FCSTD DOCUMENT  (FreeCAD 2023.731R38791 (Git))
Label: UR5e_asm
License: All rights reserved
LicenseURL: http://en.wikipedia.org/wiki/All_rights_reserved
objects: App::Link×17, App::DocumentObjectGroup×3, PartDesign::CoordinateSystem×1, App::FeaturePython×1, App::Part×1, TechDraw::DrawSVGTemplate×1, TechDraw::DrawViewPart×1, TechDraw::DrawPage×1
note: 1 computed .brp shape members not serialized (recipe doc carries the construction recipe); baked Part::Feature solids carry a one-line shape summary decoded from their .brp
EXTERNAL_REF file=parts/Hub_Offset_asm.FCStd obj=Group_Shaft
EXTERNAL_REF file=Joint_mount.FCStd obj=Hub_Bore
EXTERNAL_REF file=parts/Hub_Offset_asm.FCStd obj=Assembly
EXTERNAL_REF file=parts/Hub_Offset_asm.FCStd obj=Group_Bore0
EXTERNAL_REF file=prefab/Interconnect_shaft.FCStd obj=Local_CS
EXTERNAL_REF file=prefab/Interconnect_shaft.FCStd obj=Icon_Shaft
EXTERNAL_REF file=parts/Hub_Offset_asm.FCStd obj=Group_Bore1
EXTERNAL_REF file=parts/Hub_Mount_asm.FCStd obj=Hub_Mount_Bore1
EXTERNAL_REF file=prefab/Interconnect_shaft.FCStd obj=Local_CS001
EXTERNAL_REF file=parts/Hub_Mount_asm.FCStd obj=Assembly
EXTERNAL_REF file=parts/Hub_Mount_asm.FCStd obj=Group_Base
EXTERNAL_REF file=Joint_mount.FCStd obj=Encoder_Base
EXTERNAL_REF file=Joint_mount.FCStd obj=Assembly
EXTERNAL_REF file=parts/Hub_Offset_Direct_asm.FCStd obj=DIrect_Mount
EXTERNAL_REF file=parts/Hub_Offset_Direct_asm.FCStd obj=Assembly
EXTERNAL_REF file=parts/Hub_Offset_Direct_asm.FCStd obj=DIrect_ASM_mount
EXTERNAL_REF file=Joint_mount.FCStd obj=LCS_Origin
EXTERNAL_REF file=parts/Hub_Mount_asm.FCStd obj=Hub_Mount_Bore0

FEATURE [App::DocumentObjectGroup] Parts
  ClaimAllChildren = true
  ExportMode = 1
  TreeRank = 0
  _GroupVersion = 1
FEATURE [PartDesign::CoordinateSystem] LCS_Origin
  AttacherType = Attacher::AttachEngine3D
  AttachmentSupport = -> [X_Axis]
  InvalidShape = false
  MapMode = 2
  Support = -> [X_Axis]
  TreeRank = 0
  ValidateShape = false
FEATURE [App::DocumentObjectGroup] Constraints
  ClaimAllChildren = true
  ExportMode = 1
  TreeRank = 0
  _GroupVersion = 1
FEATURE [App::FeaturePython] Variables  # WARN: FeaturePython — macro-defined, semantics opaque (R4)
  TreeRank = 0
  Type = App::PropertyContainer
FEATURE [App::DocumentObjectGroup] Configurations
  ClaimAllChildren = true
  ExportMode = 1
  TreeRank = 0
  _GroupVersion = 1
FEATURE [App::Link] Hub_offset_asm001  label="Hub_offset_asm"
  AttachedBy = #Group_Shaft
  AttachedTo = Joint_mount001#Hub_Bore
  AttachmentOffset = pos=(0,0,0) rot=(0,0,1;3.14159rad)
  AutoLinkLabel = true
  AutoPlacement = true
  LinkPlacement = pos=(-17,-235,-0.999989) rot=(0.57735,-0.57735,0.57735;4.18879rad)
  LinkedObject = -> <external parts/Hub_Offset_asm.FCStd>#Assembly
  Placement = pos=(-17,-235,-0.999989) rot=(0.57735,-0.57735,0.57735;4.18879rad)
  SolverId = Asm4EE
  SyncGroupVisibility = false
  TreeRank = 7
  _LinkVersion = 1
  expr: Placement = Joint_mount001.Placement * Joint_mount#Hub_Bore.Placement * AttachmentOffset * Hub_Offset_asm#Group_Shaft.Placement ^ (-1)
FEATURE [App::Link] Icon_Shaft002  label="Icon_Shaft002(Icon_Shaft)"
  AttachedBy = #Local_CS
  AttachedTo = Hub_offset_asm001#Group_Bore0
  AutoLinkLabel = true
  AutoPlacement = true
  LinkPlacement = pos=(-9.50001,-217,-18) rot=(1,0,0;1.5708rad)
  LinkedObject = -> <external prefab/Interconnect_shaft.FCStd>#Icon_Shaft
  Placement = pos=(-9.50001,-217,-18) rot=(1,0,0;1.5708rad)
  SolverId = Asm4EE
  SyncGroupVisibility = false
  TreeRank = 8
  _LinkVersion = 1
  expr: Placement = Hub_offset_asm001.Placement * Hub_Offset_asm#Group_Bore0.Placement * AttachmentOffset * Interconnect_shaft#Local_CS.Placement ^ (-1)
FEATURE [App::Link] Icon_Shaft002_Icon_Shaft_  label="Icon_Shaft002(Icon_Shaft)001"
  AttachedBy = #Local_CS
  AttachedTo = Hub_offset_asm001#Group_Bore1
  AutoLinkLabel = true
  AutoPlacement = true
  LinkPlacement = pos=(-9.49999,-217,16) rot=(1,0,0;1.5708rad)
  LinkedObject = -> <external prefab/Interconnect_shaft.FCStd>#Icon_Shaft
  Placement = pos=(-9.49999,-217,16) rot=(1,0,0;1.5708rad)
  SolverId = Asm4EE
  SyncGroupVisibility = false
  TreeRank = 9
  _LinkVersion = 1
  expr: Placement = Hub_offset_asm001.Placement * Hub_Offset_asm#Group_Bore1.Placement * AttachmentOffset * Interconnect_shaft#Local_CS.Placement ^ (-1)
FEATURE [App::Link] Hub_Mount_asm001  label="Hub_Mount_asm"
  AttachedBy = #Hub_Mount_Bore1
  AttachedTo = Icon_Shaft002_Icon_Shaft_#Local_CS001
  AttachmentOffset = pos=(0,0,0) rot=(0,0,1;1.5708rad)
  AutoLinkLabel = true
  AutoPlacement = true
  LinkPlacement = pos=(8.99999e-06,-371,14) rot=(0,-1,0;4.71239rad)
  LinkedObject = -> <external parts/Hub_Mount_asm.FCStd>#Assembly
  Placement = pos=(8.99999e-06,-371,14) rot=(0,-1,0;4.71239rad)
  SolverId = Asm4EE
  SyncGroupVisibility = false
  TreeRank = 10
  _LinkVersion = 1
  expr: Placement = Icon_Shaft002_Icon_Shaft_.Placement * Interconnect_shaft#Local_CS001.Placement * AttachmentOffset * Hub_Mount_asm#Hub_Mount_Bore1.Placement ^ (-1)
FEATURE [App::Link] Joint_mount003  label="Joint_mount003(Assembly)"
  AttachedBy = #Encoder_Base
  AttachedTo = Hub_Mount_asm001#Group_Base
  AttachmentOffset = pos=(0,0,0) rot=(0,0,1;4.71239rad)
  AutoLinkLabel = true
  AutoPlacement = true
  LinkPlacement = pos=(4,-388,0.499997) rot=(0.57735,0.57735,-0.57735;2.0944rad)
  LinkedObject = -> <external Joint_mount.FCStd>#Assembly
  Placement = pos=(4,-388,0.499997) rot=(0.57735,0.57735,-0.57735;2.0944rad)
  SolverId = Asm4EE
  SyncGroupVisibility = false
  TreeRank = 16
  _LinkVersion = 1
  expr: Placement = Hub_Mount_asm001.Placement * Hub_Mount_asm#Group_Base.Placement * AttachmentOffset * Joint_mount#Encoder_Base.Placement ^ (-1)
FEATURE [App::Link] Direct_asm  label="Direct_asm(Direct_asm)"
  AttachedBy = #DIrect_Mount
  AttachedTo = Joint_mount003#Hub_Bore
  AutoLinkLabel = true
  AutoPlacement = true
  LinkPlacement = pos=(-53,-388,20.5) rot=(-0.57735,-0.57735,0.57735;2.09439rad)
  LinkedObject = -> <external parts/Hub_Offset_Direct_asm.FCStd>#Assembly
  Placement = pos=(-53,-388,20.5) rot=(-0.57735,-0.57735,0.57735;2.09439rad)
  SolverId = Asm4EE
  SyncGroupVisibility = false
  TreeRank = 19
  _LinkVersion = 1
  expr: Placement = Joint_mount003.Placement * Joint_mount#Hub_Bore.Placement * AttachmentOffset * Hub_Offset_Direct_asm#DIrect_Mount.Placement ^ (-1)
FEATURE [App::Link] Joint_mount004  label="Joint_mount004(Assembly)"
  AttachedBy = #Encoder_Base
  AttachedTo = Direct_asm#DIrect_ASM_mount
  AutoLinkLabel = true
  AutoPlacement = true
  LinkPlacement = pos=(-78,-388.5,-3.49995) rot=(-0.57735,-0.57735,0.57735;2.09439rad)
  LinkedObject = -> <external Joint_mount.FCStd>#Assembly
  Placement = pos=(-78,-388.5,-3.49995) rot=(-0.57735,-0.57735,0.57735;2.09439rad)
  SolverId = Asm4EE
  SyncGroupVisibility = false
  TreeRank = 20
  _LinkVersion = 1
  expr: Placement = Direct_asm.Placement * Hub_Offset_Direct_asm#DIrect_ASM_mount.Placement * AttachmentOffset * Joint_mount#Encoder_Base.Placement ^ (-1)
FEATURE [App::Link] Direct_asm001  label="Direct_asm"
  AttachedBy = #DIrect_Mount
  AttachedTo = Joint_mount004#Hub_Bore
  AutoLinkLabel = true
  AutoPlacement = true
  LinkPlacement = pos=(-78,-408.5,53.5) rot=(-0.57735,-0.57735,0.57735;6.28318rad)
  LinkedObject = -> <external parts/Hub_Offset_Direct_asm.FCStd>#Assembly
  Placement = pos=(-78,-408.5,53.5) rot=(-0.57735,-0.57735,0.57735;6.28318rad)
  SolverId = Asm4EE
  SyncGroupVisibility = false
  TreeRank = 21
  _LinkVersion = 1
  expr: Placement = Joint_mount004.Placement * Joint_mount#Hub_Bore.Placement * AttachmentOffset * Hub_Offset_Direct_asm#DIrect_Mount.Placement ^ (-1)
FEATURE [App::Link] Joint_mount005  label="Joint_mount005(Assembly)"
  AttachedBy = #Encoder_Base
  AttachedTo = Direct_asm001#DIrect_ASM_mount
  AutoLinkLabel = true
  AutoPlacement = true
  LinkPlacement = pos=(-78.4999,-384.5,78.5001) rot=(-0.57735,-0.57735,0.57735;6.28318rad)
  LinkedObject = -> <external Joint_mount.FCStd>#Assembly
  Placement = pos=(-78.4999,-384.5,78.5001) rot=(-0.57735,-0.57735,0.57735;6.28318rad)
  SolverId = Asm4EE
  SyncGroupVisibility = false
  TreeRank = 22
  _LinkVersion = 1
  expr: Placement = Direct_asm001.Placement * Hub_Offset_Direct_asm#DIrect_ASM_mount.Placement * AttachmentOffset * Joint_mount#Encoder_Base.Placement ^ (-1)
FEATURE [App::Link] Joint_mount006  label="Joint_mount006(Assembly)"
  AttachedBy = #LCS_Origin
  AttachedTo = Parent Assembly#LCS_Origin
  AutoLinkLabel = true
  AutoPlacement = true
  LinkedObject = -> <external Joint_mount.FCStd>#Assembly
  SolverId = Asm4EE
  SyncGroupVisibility = false
  TreeRank = 23
  _LinkVersion = 1
  expr: Placement = LCS_Origin.Placement * AttachmentOffset * Joint_mount#LCS_Origin.Placement ^ (-1)
FEATURE [App::Link] Direct_asm002  label="Direct_asm002(Direct_asm)"
  AttachedBy = #DIrect_Mount
  AttachedTo = Joint_mount006#Hub_Bore
  AutoLinkLabel = true
  AutoPlacement = true
  LinkPlacement = pos=(-20,-57,1.28571e-05) rot=(-0.57735,-0.57735,0.57735;4.18879rad)
  LinkedObject = -> <external parts/Hub_Offset_Direct_asm.FCStd>#Assembly
  Placement = pos=(-20,-57,1.28571e-05) rot=(-0.57735,-0.57735,0.57735;4.18879rad)
  SolverId = Asm4EE
  SyncGroupVisibility = false
  TreeRank = 24
  _LinkVersion = 1
  expr: Placement = Joint_mount006.Placement * Joint_mount#Hub_Bore.Placement * AttachmentOffset * Hub_Offset_Direct_asm#DIrect_Mount.Placement ^ (-1)
FEATURE [App::Link] Joint_mount  label="Joint_mount(Assembly)"
  AttachedBy = #Encoder_Base
  AttachedTo = Direct_asm002#DIrect_ASM_mount
  AutoLinkLabel = true
  AutoPlacement = true
  LinkPlacement = pos=(4,-82,0.499997) rot=(-0.57735,-0.57735,0.57735;4.18879rad)
  LinkedObject = -> <external Joint_mount.FCStd>#Assembly
  Placement = pos=(4,-82,0.499997) rot=(-0.57735,-0.57735,0.57735;4.18879rad)
  SolverId = Asm4EE
  SyncGroupVisibility = false
  TreeRank = 25
  _LinkVersion = 1
  expr: Placement = Direct_asm002.Placement * Hub_Offset_Direct_asm#DIrect_ASM_mount.Placement * AttachmentOffset * Joint_mount#Encoder_Base.Placement ^ (-1)
FEATURE [App::Link] Hub_offset_asm  label="Hub_offset_asm(Hub_offset_asm)"
  AttachedBy = #Group_Shaft
  AttachedTo = Joint_mount#Hub_Bore
  AttachmentOffset = pos=(0,0,0) rot=(0,0,1;3.14159rad)
  AutoLinkLabel = true
  AutoPlacement = true
  LinkPlacement = pos=(-53,-82,0.500034) rot=(0.57735,-0.57735,-0.577351;2.0944rad)
  LinkedObject = -> <external parts/Hub_Offset_asm.FCStd>#Assembly
  Placement = pos=(-53,-82,0.500034) rot=(0.57735,-0.57735,-0.577351;2.0944rad)
  SolverId = Asm4EE
  SyncGroupVisibility = false
  TreeRank = 26
  _LinkVersion = 1
  expr: Placement = Joint_mount.Placement * Joint_mount#Hub_Bore.Placement * AttachmentOffset * Hub_Offset_asm#Group_Shaft.Placement ^ (-1)
FEATURE [App::Link] Icon_Shaft  label="Icon_Shaft(Icon_Shaft)"
  AttachedBy = #Local_CS
  AttachedTo = Hub_offset_asm#Group_Bore0
  AutoLinkLabel = true
  AutoPlacement = true
  LinkPlacement = pos=(-60.5,-64,17.5) rot=(0,0.707107,-0.707107;3.14159rad)
  LinkedObject = -> <external prefab/Interconnect_shaft.FCStd>#Icon_Shaft
  Placement = pos=(-60.5,-64,17.5) rot=(0,0.707107,-0.707107;3.14159rad)
  SolverId = Asm4EE
  SyncGroupVisibility = false
  TreeRank = 27
  _LinkVersion = 1
  expr: Placement = Hub_offset_asm.Placement * Hub_Offset_asm#Group_Bore0.Placement * AttachmentOffset * Interconnect_shaft#Local_CS.Placement ^ (-1)
FEATURE [App::Link] Icon_Shaft001  label="Icon_Shaft"
  AttachedBy = #Local_CS
  AttachedTo = Hub_offset_asm#Group_Bore1
  AutoLinkLabel = true
  AutoPlacement = true
  LinkPlacement = pos=(-60.5,-64,-16.5) rot=(0,0.707107,-0.707107;3.14159rad)
  LinkedObject = -> <external prefab/Interconnect_shaft.FCStd>#Icon_Shaft
  Placement = pos=(-60.5,-64,-16.5) rot=(0,0.707107,-0.707107;3.14159rad)
  SolverId = Asm4EE
  SyncGroupVisibility = false
  TreeRank = 28
  _LinkVersion = 1
  expr: Placement = Hub_offset_asm.Placement * Hub_Offset_asm#Group_Bore1.Placement * AttachmentOffset * Interconnect_shaft#Local_CS.Placement ^ (-1)
FEATURE [App::Link] Hub_Mount_asm  label="Hub_Mount_asm(Assembly)"
  AttachedBy = #Hub_Mount_Bore0
  AttachedTo = Icon_Shaft#Local_CS001
  AttachmentOffset = pos=(0,0,0) rot=(0,0,1;1.5708rad)
  AutoLinkLabel = true
  AutoPlacement = true
  LinkPlacement = pos=(-70,-218,-14.5) rot=(0,-1,0;1.5708rad)
  LinkedObject = -> <external parts/Hub_Mount_asm.FCStd>#Assembly
  Placement = pos=(-70,-218,-14.5) rot=(0,-1,0;1.5708rad)
  SolverId = Asm4EE
  SyncGroupVisibility = false
  TreeRank = 29
  _LinkVersion = 1
  expr: Placement = Icon_Shaft.Placement * Interconnect_shaft#Local_CS001.Placement * AttachmentOffset * Hub_Mount_asm#Hub_Mount_Bore0.Placement ^ (-1)
FEATURE [App::Link] Joint_mount001  label="Joint_mount"
  AttachedBy = #Encoder_Base
  AttachedTo = Hub_Mount_asm#Group_Base
  AttachmentOffset = pos=(0,0,0) rot=(0,0,1;4.71239rad)
  AutoLinkLabel = true
  AutoPlacement = true
  LinkPlacement = pos=(-74,-235,-0.999952) rot=(-0.577351,0.57735,-0.57735;4.18879rad)
  LinkedObject = -> <external Joint_mount.FCStd>#Assembly
  Placement = pos=(-74,-235,-0.999952) rot=(-0.577351,0.57735,-0.57735;4.18879rad)
  SolverId = Asm4EE
  SyncGroupVisibility = false
  TreeRank = 30
  _LinkVersion = 1
  expr: Placement = Hub_Mount_asm.Placement * Hub_Mount_asm#Group_Base.Placement * AttachmentOffset * Joint_mount#Encoder_Base.Placement ^ (-1)
FEATURE [App::Part] Assembly
  AssemblyType = Part::Link
  ClaimAllChildren = false
  ExportMode = 1
  Group = -> [LCS_Origin,Constraints,Variables,Configurations,Joint_mount,Hub_offset_asm,Icon_Shaft,Icon_Shaft001,Hub_Mount_asm,Joint_mount001,Hub_offset_asm001,Icon_Shaft002,Icon_Shaft002_Icon_Shaft_,Hub_Mount_asm001,Joint_mount003,Direct_asm,Joint_mount004,Direct_asm001,Joint_mount005,Joint_mount006,Direct_asm002]
  Origin = -> Origin
  TreeRank = 0
  Type = Assembly
  _ExportChildren = -> [LCS_Origin,Constraints,Variables,Configurations,Joint_mount,Hub_offset_asm,Icon_Shaft,Icon_Shaft001,Hub_Mount_asm,Joint_mount001,Hub_offset_asm001,Icon_Shaft002,Icon_Shaft002_Icon_Shaft_,Hub_Mount_asm001,Joint_mount003,Direct_asm,Joint_mount004,Direct_asm001,Joint_mount005,Joint_mount006,Direct_asm002]
  _GroupVersion = 1
FEATURE [TechDraw::DrawSVGTemplate] Template
  EditableTexts = APPROVER_NAME=APPROVER NAME; AUTHOR_NAME=AUTHOR NAME; DATE=YYYY-MM-DD; DN=DN; DOCUMENT_TYPE=Mechanical assembly drawing; OWNER_NAME=OWNER NAME; PM=PM; PN=PN; REVISION=REV A; RIGHTS=(R) DO NOT DUPLICATE THIS DRAWING TO THIRD PARTIES WITHOUT OWNER'S PERMISSION !; SCALE=M x:x; SHEET=99 of 99; SIZE=A2; TITLELINE-1=FreeCAD; TOLERANCE=+/- ?
  Height = 420
  Orientation = 1
  Template = /app/share/Mod/TechDraw/Templates/A2_Landscape_ISO7200_Pep.svg
  TreeRank = 32
  Width = 594
FEATURE [TechDraw::DrawViewPart] View
  CoarseView = false
  Direction = (0,0,1)
  Focus = 100
  HardHidden = false
  IsoCount = 0
  IsoHidden = false
  IsoVisible = false
  LockPosition = false
  Perspective = false
  Rotation = 0
  ScaleType = 0
  ScrubCount = 0
  SeamHidden = false
  SeamVisible = true
  SmoothHidden = false
  SmoothVisible = true
  Source = -> [Assembly]
  TreeRank = 34
  X = 297
  XDirection = (0,-1,0)
  Y = 210
FEATURE [TechDraw::DrawPage] Page
  KeepUpdated = true
  NextBalloonIndex = 1
  ProjectionType = 0
  Template = -> Template
  TreeRank = 33
  Views = -> [View]

RESOLVED EXTERNAL PARTS (link-assembly join: the EXTERNAL_REF files above that resolve inside this repo's crawl, each included once):
---- part Joint_mount.FCStd = doc fcstd_61794816e52a ----
FCSTD DOCUMENT  (FreeCAD 2023.521R14555 (Git shallow))
Label: Joint_mount
License: All rights reserved
objects: App::Link×8, App::DocumentObjectGroup×3, PartDesign::CoordinateSystem×3, App::FeaturePython×1, App::Part×1
note: 3 computed .brp shape members not serialized (recipe doc carries the construction recipe); baked Part::Feature solids carry a one-line shape summary decoded from their .brp
EXTERNAL_REF file=parts/spark_encoder_mount.FCStd obj=Home
EXTERNAL_REF file=parts/spark_encoder_mount.FCStd obj=Part
EXTERNAL_REF file=prefab/Bearing_6x16x4.FCStd obj=Local_CS
EXTERNAL_REF file=parts/spark_encoder_mount.FCStd obj=Bearing0
EXTERNAL_REF file=prefab/Bearing_6x16x4.FCStd obj=Part
EXTERNAL_REF file=parts/spark_encoder_mount.FCStd obj=Local_CS
EXTERNAL_REF file=prefab/Shaft.FCStd obj=LCS_1
EXTERNAL_REF file=prefab/Shaft.FCStd obj=Part
EXTERNAL_REF file=prefab/Bearing_6x16x4.FCStd obj=Local_CS001
EXTERNAL_REF file=prefab/Hub_6.FCStd obj=Face
EXTERNAL_REF file=prefab/Hub_6.FCStd obj=Part
EXTERNAL_REF file=prefab/Collar_6x19x9.FCStd obj=LCS_1
EXTERNAL_REF file=prefab/Collar_6x19x9.FCStd obj=Part
EXTERNAL_REF file=parts/spark_mag_holder.FCStd obj=LCS_1
EXTERNAL_REF file=parts/spark_mag_holder.FCStd obj=Mag_holder
EXTERNAL_REF file=prefab/Magnet.FCStd obj=LCS_1
EXTERNAL_REF file=parts/spark_mag_holder.FCStd obj=LCS_2
EXTERNAL_REF file=prefab/Magnet.FCStd obj=Body
EXTERNAL_REF file=prefab/Hub_6.FCStd obj=Bore
EXTERNAL_REF file=parts/spark_encoder_mount.FCStd obj=Base

FEATURE [App::DocumentObjectGroup] Parts
  ClaimAllChildren = true
  ExportMode = 1
  TreeRank = 12
  _GroupVersion = 1
FEATURE [PartDesign::CoordinateSystem] LCS_Origin
  AttacherType = Attacher::AttachEngine3D
  AttachmentSupport = -> [X_Axis]
  InvalidShape = false
  MapMode = 2
  Support = -> [X_Axis]
  TreeRank = 4
  ValidateShape = false
FEATURE [App::DocumentObjectGroup] Constraints
  ClaimAllChildren = true
  ExportMode = 1
  TreeRank = 11
  _GroupVersion = 1
FEATURE [App::FeaturePython] Variables  # WARN: FeaturePython — macro-defined, semantics opaque (R4)
  TreeRank = 17
  Type = App::PropertyContainer
FEATURE [App::DocumentObjectGroup] Configurations
  ClaimAllChildren = true
  ExportMode = 1
  TreeRank = 18
  _GroupVersion = 1
FEATURE [App::Link] Encoder  label="Encoder(Encoder)"
  AttachedBy = #Home
  AttachedTo = Parent Assembly#LCS_Origin
  AttachmentOffset = pos=(0,0,0) rot=(-0.57735,0.57735,-0.57735;4.18879rad)
  AutoLinkLabel = true
  AutoPlacement = true
  LinkPlacement = pos=(0,0,0) rot=(0,0,1;4.71239rad)
  LinkedObject = -> <external parts/spark_encoder_mount.FCStd>#Part
  Placement = pos=(0,0,0) rot=(0,0,1;4.71239rad)
  SolverId = Asm4EE
  SyncGroupVisibility = false
  TreeRank = 19
  _LinkVersion = 1
  expr: Placement = LCS_Origin.Placement * AttachmentOffset * spark_encoder_mount#Home.Placement ^ (-1)
FEATURE [App::Link] Bearing  label="Bearing(Bearing)"
  AttachedBy = #Local_CS
  AttachedTo = Encoder#Bearing0
  AutoLinkLabel = true
  AutoPlacement = true
  LinkPlacement = pos=(-4.2e-15,-20,1.29e-14) rot=(0.707107,0,0.707107;3.14159rad)
  LinkedObject = -> <external prefab/Bearing_6x16x4.FCStd>#Part
  Placement = pos=(-4.2e-15,-20,1.29e-14) rot=(0.707107,0,0.707107;3.14159rad)
  SolverId = Asm4EE
  SyncGroupVisibility = false
  TreeRank = 20
  _LinkVersion = 1
  expr: Placement = Encoder.Placement * spark_encoder_mount#Bearing0.Placement * AttachmentOffset * Bearing_6x16x4#Local_CS.Placement ^ (-1)
FEATURE [App::Link] Bearing001  label="Bearing"
  AttachedBy = #Local_CS
  AttachedTo = Encoder#Local_CS
  AutoLinkLabel = true
  AutoPlacement = true
  LinkPlacement = pos=(-9.8e-15,-47,3.27e-14) rot=(0,1,0;1.5708rad)
  LinkedObject = -> <external prefab/Bearing_6x16x4.FCStd>#Part
  Placement = pos=(-9.8e-15,-47,3.27e-14) rot=(0,1,0;1.5708rad)
  SolverId = Asm4EE
  SyncGroupVisibility = false
  TreeRank = 21
  _LinkVersion = 1
  expr: Placement = Encoder.Placement * spark_encoder_mount#Local_CS.Placement * AttachmentOffset * Bearing_6x16x4#Local_CS.Placement ^ (-1)
FEATURE [App::Link] Shaft  label="Shaft(Shaft)"
  AttachedBy = #LCS_1
  AttachedTo = Encoder#Home
  AttachmentOffset = pos=(0,0,6) rot=(0,0,1;0rad)
  AutoLinkLabel = true
  AutoPlacement = true
  LinkPlacement = pos=(7e-16,-6,3.3e-15) rot=(0,0,1;0rad)
  LinkedObject = -> <external prefab/Shaft.FCStd>#Part
  Placement = pos=(7e-16,-6,3.3e-15) rot=(0,0,1;0rad)
  SolverId = Asm4EE
  SyncGroupVisibility = false
  TreeRank = 22
  _LinkVersion = 1
  expr: Placement = Encoder.Placement * spark_encoder_mount#Home.Placement * AttachmentOffset * Shaft#LCS_1.Placement ^ (-1)
FEATURE [App::Link] Hub  label="Hub(Hub)"
  AttachedBy = #Face
  AttachedTo = Bearing001#Local_CS001
  AutoLinkLabel = true
  AutoPlacement = true
  LinkPlacement = pos=(-4.97356,-54.3025,-1.29993) rot=(0,-0.707107,-0.707107;3.14159rad)
  LinkedObject = -> <external prefab/Hub_6.FCStd>#Part
  Placement = pos=(-4.97356,-54.3025,-1.29993) rot=(0,-0.707107,-0.707107;3.14159rad)
  SolverId = Asm4EE
  SyncGroupVisibility = false
  TreeRank = 23
  _LinkVersion = 1
  expr: Placement = Bearing001.Placement * Bearing_6x16x4#Local_CS001.Placement * AttachmentOffset * Hub_6#Face.Placement ^ (-1)
FEATURE [App::Link] Collar  label="Collar(Collar)"
  AttachedBy = #LCS_1
  AttachedTo = Bearing#Local_CS001
  AutoLinkLabel = true
  AutoPlacement = true
  LinkPlacement = pos=(-24.7535,-15.5204,25.1307) rot=(0.6,0,0.8;3.14159rad)
  LinkedObject = -> <external prefab/Collar_6x19x9.FCStd>#Part
  Placement = pos=(-24.7535,-15.5204,25.1307) rot=(0.6,0,0.8;3.14159rad)
  SolverId = Asm4EE
  SyncGroupVisibility = false
  TreeRank = 24
  _LinkVersion = 1
  expr: Placement = Bearing.Placement * Bearing_6x16x4#Local_CS001.Placement * AttachmentOffset * Collar_6x19x9#LCS_1.Placement ^ (-1)
FEATURE [App::Link] Mag_holder  label="Mag_holder(Mag_holder)"
  AttachedBy = #LCS_1
  AttachedTo = Shaft#LCS_1
  AutoLinkLabel = true
  AutoPlacement = true
  LinkPlacement = pos=(2e-16,-10,5.1e-15) rot=(-0.57735,0.57735,0.57735;4.18879rad)
  LinkedObject = -> <external parts/spark_mag_holder.FCStd>#Mag_holder
  Placement = pos=(2e-16,-10,5.1e-15) rot=(-0.57735,0.57735,0.57735;4.18879rad)
  SolverId = Asm4EE
  SyncGroupVisibility = false
  TreeRank = 25
  _LinkVersion = 1
  expr: Placement = Shaft.Placement * Shaft#LCS_1.Placement * AttachmentOffset * spark_mag_holder#LCS_1.Placement ^ (-1)
FEATURE [App::Link] Magnet  label="Magnet(Magnet)"
  AttachedBy = #LCS_1
  AttachedTo = Mag_holder#LCS_2
  AttachmentOffset = pos=(0,0,0) rot=(1,0,0;3.14159rad)
  AutoLinkLabel = true
  AutoPlacement = true
  LinkPlacement = pos=(1.2e-15,-1.325,1.3e-15) rot=(-0.57735,0.57735,-0.57735;2.0944rad)
  LinkedObject = -> <external prefab/Magnet.FCStd>#Body
  Placement = pos=(1.2e-15,-1.325,1.3e-15) rot=(-0.57735,0.57735,-0.57735;2.0944rad)
  SolverId = Asm4EE
  SyncGroupVisibility = false
  TreeRank = 26
  _LinkVersion = 1
  expr: Placement = Mag_holder.Placement * spark_mag_holder#LCS_2.Placement * AttachmentOffset * Magnet#LCS_1.Placement ^ (-1)
FEATURE [PartDesign::CoordinateSystem] Hub_Bore
  AttachedBy = Origin
  AttacherType = Attacher::AttachEngine3D
  InvalidShape = false
  Placement = pos=(-1.33e-14,-57,3.69e-14) rot=(-0.57735,-0.57735,0.57735;4.18879rad)
  SolverId = Asm4EE
  TreeRank = 27
  ValidateShape = false
  expr: Placement = Hub.Placement * Hub_6#Bore.Placement
FEATURE [PartDesign::CoordinateSystem] Encoder_Base
  AttachedBy = Origin
  AttacherType = Attacher::AttachEngine3D
  InvalidShape = false
  Placement = pos=(-13.5,-4,-17) rot=(0,0,1;0rad)
  SolverId = Asm4EE
  TreeRank = 28
  ValidateShape = false
  expr: Placement = Encoder.Placement * spark_encoder_mount#Base.Placement
FEATURE [App::Part] Assembly
  AssemblyType = Part::Link
  ClaimAllChildren = false
  ExportMode = 1
  Group = -> [LCS_Origin,Constraints,Variables,Configurations,Encoder,Bearing,Bearing001,Shaft,Hub,Collar,Mag_holder,Magnet,Hub_Bore,Encoder_Base]
  Origin = -> Origin
  TreeRank = 14
  Type = Assembly
  _ExportChildren = -> [LCS_Origin,Constraints,Variables,Configurations,Encoder,Bearing,Bearing001,Shaft,Hub,Collar,Mag_holder,Magnet,Hub_Bore,Encoder_Base]
  _GroupVersion = 1
---- part prefab/Interconnect_shaft.FCStd = doc fcstd_2bef234e055f ----
FCSTD DOCUMENT  (FreeCAD 2023.521R14555 (Git shallow))
Label: Interconnect_shaft
License: All rights reserved
LicenseURL: http://en.wikipedia.org/wiki/All_rights_reserved
objects: PartDesign::CoordinateSystem×2, Sketcher::SketchObject×1, PartDesign::Pad×1, PartDesign::Body×1, App::FeaturePython×1, App::Part×1
note: 8 computed .brp shape members not serialized (recipe doc carries the construction recipe); baked Part::Feature solids carry a one-line shape summary decoded from their .brp

FEATURE [Sketcher::SketchObject] Sketch
  ArcFitTolerance = 0
  AttachmentSupport = -> [XY_Plane001]
  ExternalBSplineMaxDegree = 0
  ExternalBSplineTolerance = 0
  FullyConstrained = true
  InternalTolerance = 1e-06
  InvalidShape = false
  MakeInternals = false
  MapMode = 5
  Support = -> [XY_Plane001]
  TreeRank = 0
  ValidateShape = false
  sketch-geometry (1):
    g0: Circle CenterX=0 CenterY=0 CenterZ=0 NormalX=0 NormalY=0 NormalZ=1 AngleXU=0 Radius=5.5
  constraints (2):
    c: Coincident(g0,g-1)
    c: Diameter(g0) = 11
FEATURE [PartDesign::Pad] Pad
  AddSubType = 0
  AutoTaperInnerAngle = true
  CheckUpToFaceLimits = true
  ClaimChildren = false
  Direction = (0,0,1)
  Fit = 0
  FitJoin = 0
  InnerFit = 0
  InnerFitJoin = 0
  InvalidShape = false
  Length = 150
  Length2 = 10
  NewSolid = false
  Profile = -> Sketch
  ReferenceAxis = -> Sketch [N_Axis]
  Suppress = false
  TaperInnerAngle = 0
  TaperInnerAngleRev = 0
  TreeRank = 0
  Type = 0
  ValidateShape = true
  _ProfileBasedVersion = 0
  expr: Length = Variables.Con_Len
FEATURE [PartDesign::Body] Body
  AutoGroupSolids = false
  ClaimAllChildren = false
  ExportMode = 0
  Group = -> [Sketch,Pad]
  InvalidShape = false
  Origin = -> Origin001
  Tip = -> Pad
  TreeRank = 0
  ValidateShape = false
  _ExportChildren = -> [Pad]
  _GroupVersion = 1
FEATURE [App::FeaturePython] Variables  # WARN: FeaturePython — macro-defined, semantics opaque (R4)
  Con_Len = 150
  TreeRank = 0
  Type = App::PropertyContainer
FEATURE [PartDesign::CoordinateSystem] Local_CS  label="Start"
  AttacherType = Attacher::AttachEngine3D
  AttachmentSupport = -> [Pad]
  InvalidShape = false
  MapMode = 11
  Placement = pos=(0,0,0) rot=(0,0,1;1.5708rad)
  Support = -> [Pad]
  TreeRank = 1
  ValidateShape = false
FEATURE [PartDesign::CoordinateSystem] Local_CS001  label="End"
  AttacherType = Attacher::AttachEngine3D
  AttachmentSupport = -> [Pad]
  InvalidShape = false
  MapMode = 11
  Placement = pos=(0,0,150) rot=(0,0,1;1.5708rad)
  Support = -> [Pad]
  TreeRank = 2
  ValidateShape = false
FEATURE [App::Part] Icon_Shaft
  ClaimAllChildren = false
  ExportMode = 1
  Group = -> [Body,Local_CS,Local_CS001]
  Origin = -> Origin
  TreeRank = 0
  _ExportChildren = -> [Body,Local_CS,Local_CS001]
  _GroupVersion = 1
